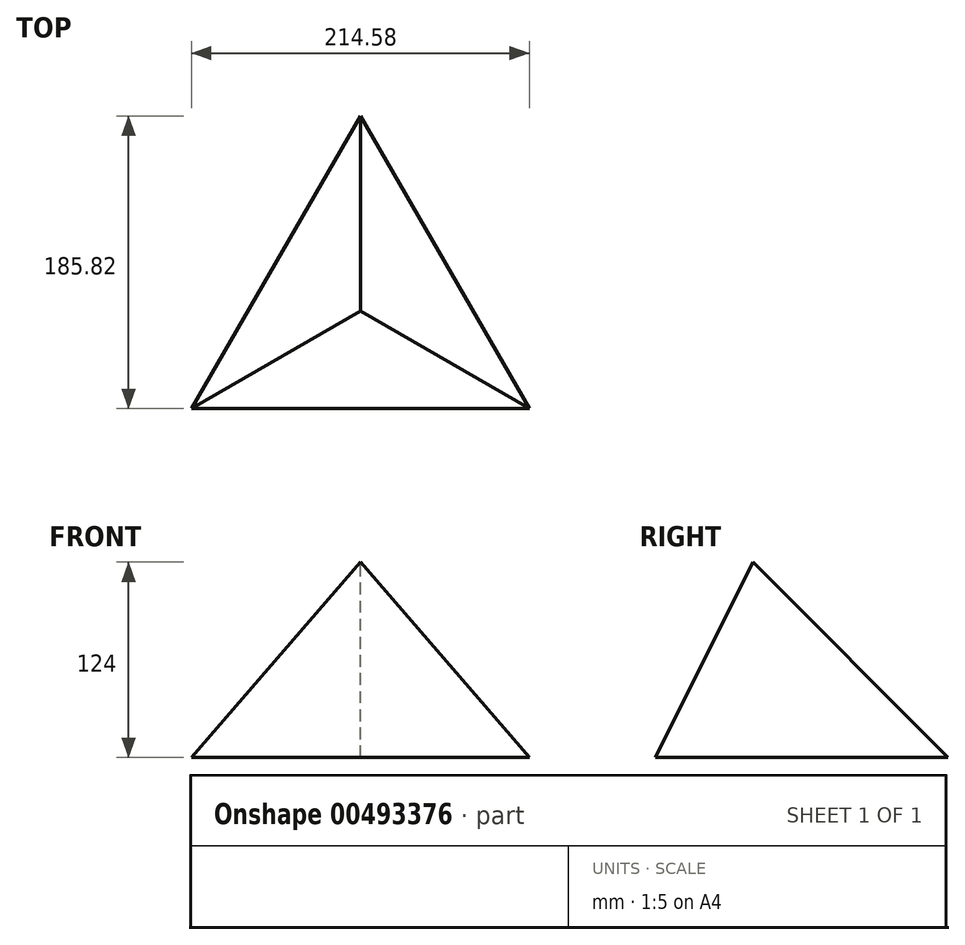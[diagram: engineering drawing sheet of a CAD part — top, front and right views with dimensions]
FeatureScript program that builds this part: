
annotation { "Feature Type Name" : "Feature", "Feature Type Description" : "" }
export const myFeature = defineFeature(function(context is Context, id is Id, definition is map)
    precondition{}
    {
        {
            var Q0;
            Q0=qCreatedBy(makeId("Top.planeOp"),FACE);
            var sketch = newSketch(context, id + "F0", { "sketchPlane" : qUnion([Q0])});
            skCircle(sketch, "E0.cCircle", {"center": v(0, 0) * mm, "radius": 123.88 * mm, "construction": true});
            skLineSegment(sketch, "E0.0", {"start": v(0, 123.88) * mm, "end": v(107.29, -61.94) * mm});
            skLineSegment(sketch, "E0.1", {"start": v(107.29, -61.94) * mm, "end": v(-107.29, -61.94) * mm});
            skLineSegment(sketch, "E0.2", {"start": v(-107.29, -61.94) * mm, "end": v(0, 123.88) * mm});
            skSolve(sketch);
        }
        {
            var Q0;
            Q0=qCreatedBy(makeId("Top.planeOp"),FACE);
            cPlane(context, id + "F1", {"entities" : qUnion([Q0]), "cplaneType" : CPlaneType.OFFSET, "offset" : 124 * mm, "width" : 150 * mm, "height" : 150 * mm});
        }
        {
            var Q0;
            Q0=qCreatedBy(id+"F1.planeOp",FACE);
            var sketch = newSketch(context, id + "F2", { "sketchPlane" : qUnion([Q0])});
            skPoint(sketch, "E1", {"position": v(0, 0) * mm});
            skSolve(sketch);
        }
        {
            var Q0;
            Q0=makeQuery(id+"F0.imprint","IMPRINT",FACE,{"disambiguationData":[TD([[makeQuery(id+"F0.imprint","IMPRINT",EDGE,{"derivedFrom":sQuery(id+"F0.wireOp",EDGE,"E0.0")}),-1.0]])]});
            var Q1;
            Q1=sQuery(id+"F2.wireOp",VERTEX,"E1");
            loft(context, id + "F3", {"sheetProfilesArray" : [{ "sheetProfileEntities" : qUnion([Q0]) }, { "sheetProfileEntities" : qUnion([Q1]) }]});
        }
    });
